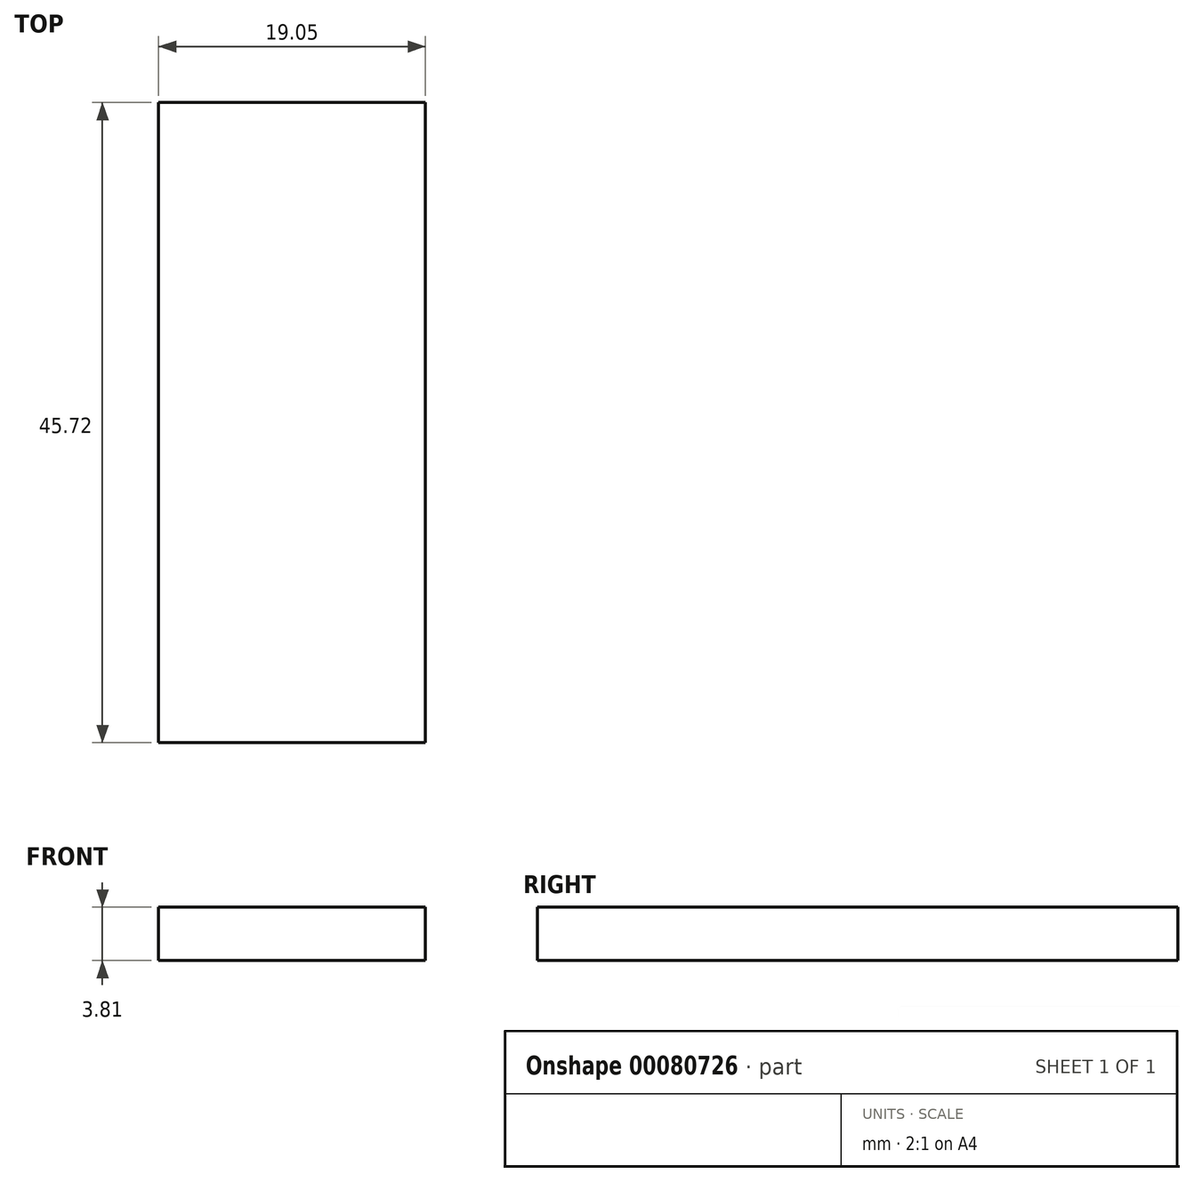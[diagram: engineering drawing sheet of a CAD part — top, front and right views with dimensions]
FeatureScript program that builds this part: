
annotation { "Feature Type Name" : "Feature", "Feature Type Description" : "" }
export const myFeature = defineFeature(function(context is Context, id is Id, definition is map)
    precondition{}
    {
        {
            var Q0;
            Q0=qCreatedBy(makeId("Top.planeOp"),FACE);
            var sketch = newSketch(context, id + "F0", { "sketchPlane" : qUnion([Q0])});
            skLineSegment(sketch, "E0.bottom", {"start": v(-15.55, 49.7) * mm, "end": v(3.5, 49.7) * mm});
            skLineSegment(sketch, "E0.top", {"start": v(-15.55, 3.99) * mm, "end": v(3.5, 3.99) * mm});
            skLineSegment(sketch, "E0.left", {"start": v(-15.55, 49.7) * mm, "end": v(-15.55, 3.99) * mm});
            skLineSegment(sketch, "E0.right", {"start": v(3.5, 49.7) * mm, "end": v(3.5, 3.99) * mm});
            skSolve(sketch);
        }
        {
            var Q0;
            Q0=makeQuery(id+"F0.imprint","IMPRINT",FACE,{"disambiguationData":[TD([[makeQuery(id+"F0.imprint","IMPRINT",EDGE,{"derivedFrom":sQuery(id+"F0.wireOp",EDGE,"E0.bottom")}),-1.0]])]});
            extrude(context, id + "F1", {"entities" : qUnion([Q0]), "depth" : 3.8 * mm});
        }
    });
